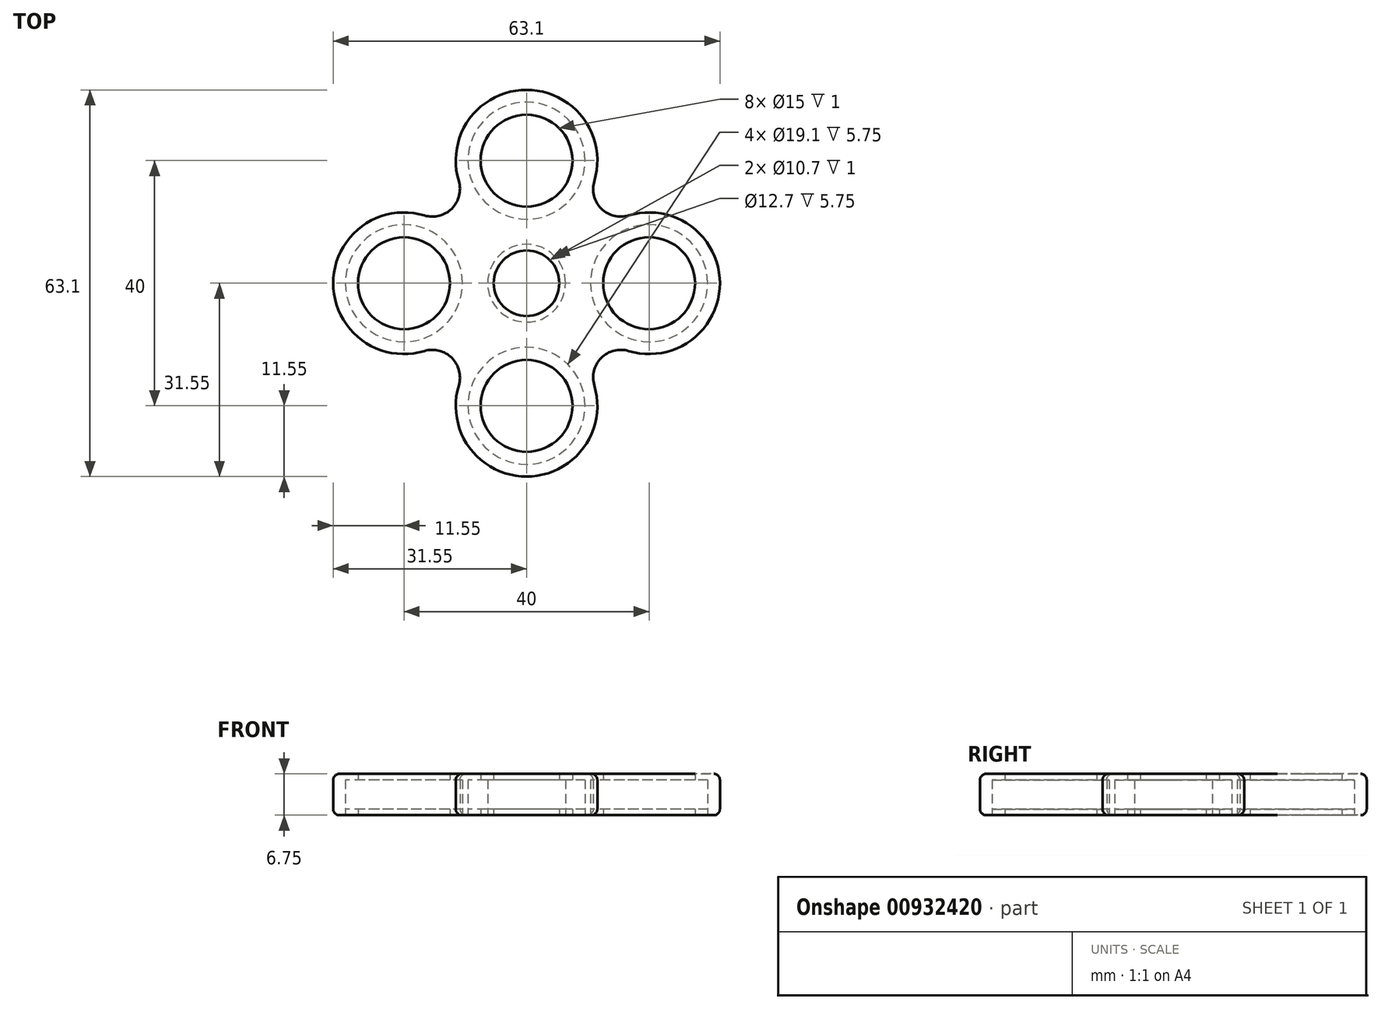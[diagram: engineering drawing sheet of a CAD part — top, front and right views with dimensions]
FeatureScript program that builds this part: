
annotation { "Feature Type Name" : "Feature", "Feature Type Description" : "" }
export const myFeature = defineFeature(function(context is Context, id is Id, definition is map)
    precondition{}
    {
        {
            var Q0;
            Q0=qCreatedBy(makeId("Top.planeOp"),FACE);
            var sketch = newSketch(context, id + "F0", { "sketchPlane" : qUnion([Q0])});
            skCircle(sketch, "E0", {"center": v(0, 0) * mm, "radius": 6.35 * mm});
            skCircle(sketch, "E1", {"center": v(0, 0) * mm, "radius": 5.35 * mm});
            skCircle(sketch, "E2.cCircle", {"center": v(0, 0) * mm, "radius": 20 * mm, "construction": true});
            skPoint(sketch, "E2.0.midPoint", {"position": v(20, 0) * mm});
            skCircle(sketch, "E3", {"center": v(-20, 0) * mm, "radius": 9.55 * mm});
            skCircle(sketch, "E4", {"center": v(0, 20) * mm, "radius": 9.55 * mm});
            skCircle(sketch, "E5", {"center": v(20, 0) * mm, "radius": 9.55 * mm});
            skCircle(sketch, "E6", {"center": v(0, -20) * mm, "radius": 9.55 * mm});
            skCircle(sketch, "E7", {"center": v(0, 20) * mm, "radius": 11.55 * mm});
            skCircle(sketch, "E8", {"center": v(-20, 0) * mm, "radius": 11.55 * mm});
            skCircle(sketch, "E9", {"center": v(0, -20) * mm, "radius": 11.55 * mm});
            skCircle(sketch, "E10", {"center": v(20, 0) * mm, "radius": 11.55 * mm});
            skArc(sketch, "E11", {"start": v(-16.66, 11.06) * mm, "mid": v(-12.18, 12.18) * mm, "end": v(-11.06, 16.66) * mm});
            skArc(sketch, "E12", {"start": v(-11.06, -16.66) * mm, "mid": v(-12.18, -12.18) * mm, "end": v(-16.66, -11.06) * mm});
            skArc(sketch, "E13", {"start": v(16.66, -11.06) * mm, "mid": v(12.18, -12.18) * mm, "end": v(11.06, -16.66) * mm});
            skArc(sketch, "E14", {"start": v(11.06, 16.66) * mm, "mid": v(12.18, 12.18) * mm, "end": v(16.66, 11.06) * mm});
            skPoint(sketch, "E15.orphan", {"position": v(-20, 20) * mm});
            skPoint(sketch, "E16.orphan", {"position": v(20, 20) * mm});
            skPoint(sketch, "E17.orphan", {"position": v(-20, -20) * mm});
            skPoint(sketch, "E18.orphan", {"position": v(20, -20) * mm});
            skCircle(sketch, "E19", {"center": v(0, 20) * mm, "radius": 7.5 * mm});
            skCircle(sketch, "E20", {"center": v(20, 0) * mm, "radius": 7.5 * mm});
            skCircle(sketch, "E21", {"center": v(0, -20) * mm, "radius": 7.5 * mm});
            skCircle(sketch, "E22", {"center": v(-20, 0) * mm, "radius": 7.5 * mm});
            skSolve(sketch);
        }
        {
            var Q0;
            Q0=makeQuery(id+"F0.imprint","IMPRINT",FACE,{"disambiguationData":[TD([[makeQuery(id+"F0.imprint","IMPRINT",EDGE,{"derivedFrom":sQuery(id+"F0.wireOp",EDGE,"E3")}),1.0]])]});
            var Q1;
            Q1=makeQuery(id+"F0.imprint","IMPRINT",FACE,{"disambiguationData":[TD([[makeQuery(id+"F0.imprint","IMPRINT",EDGE,{"derivedFrom":sQuery(id+"F0.wireOp",EDGE,"E4")}),1.0]])]});
            var Q2;
            Q2=makeQuery(id+"F0.imprint","IMPRINT",FACE,{"disambiguationData":[TD([[makeQuery(id+"F0.imprint","IMPRINT",EDGE,{"derivedFrom":sQuery(id+"F0.wireOp",EDGE,"E5")}),1.0]])]});
            var Q3;
            Q3=makeQuery(id+"F0.imprint","IMPRINT",FACE,{"disambiguationData":[TD([[makeQuery(id+"F0.imprint","IMPRINT",EDGE,{"derivedFrom":sQuery(id+"F0.wireOp",EDGE,"E6")}),1.0]])]});
            var Q4;
            Q4=makeQuery(id+"F0.imprint","IMPRINT",FACE,{"disambiguationData":[TD([[makeQuery(id+"F0.imprint","IMPRINT",EDGE,{"derivedFrom":sQuery(id+"F0.wireOp",EDGE,"E0")}),1.0]])]});
            extrude(context, id + "F1", {"entities" : qUnion([Q0, Q1, Q2, Q3, Q4]), "depth" : 1 * mm, "offsetDistance" : 25 * mm});
        }
        {
            var Q0;
            Q0=makeQuery(id+"F0.imprint","IMPRINT",FACE,{"disambiguationData":[TD([[makeQuery(id+"F0.imprint","IMPRINT",EDGE,{"derivedFrom":sQuery(id+"F0.wireOp",EDGE,"E0")}),-1.0]])]});
            var Q1;
            Q1=makeQuery(id+"F0.imprint","IMPRINT",FACE,{"disambiguationData":[TD([[makeQuery(id+"F0.imprint","IMPRINT",EDGE,{"derivedFrom":sQuery(id+"F0.wireOp",EDGE,"E3")}),-1.0]])]});
            var Q2;
            Q2=makeQuery(id+"F0.imprint","IMPRINT",FACE,{"disambiguationData":[TD([[makeQuery(id+"F0.imprint","IMPRINT",EDGE,{"derivedFrom":sQuery(id+"F0.wireOp",EDGE,"E4")}),-1.0]])]});
            var Q3;
            Q3=makeQuery(id+"F0.imprint","IMPRINT",FACE,{"disambiguationData":[TD([[makeQuery(id+"F0.imprint","IMPRINT",EDGE,{"derivedFrom":sQuery(id+"F0.wireOp",EDGE,"E5")}),-1.0]])]});
            var Q4;
            Q4=makeQuery(id+"F0.imprint","IMPRINT",FACE,{"disambiguationData":[TD([[makeQuery(id+"F0.imprint","IMPRINT",EDGE,{"derivedFrom":sQuery(id+"F0.wireOp",EDGE,"E6")}),-1.0]])]});
            extrude(context, id + "F2", {"entities" : qUnion([Q0, Q1, Q2, Q3, Q4]), "depth" : 6.75 * mm, "offsetDistance" : 25 * mm});
        }
        {
            var Q0;
            Q0=makeQuery(id+"F2.opExtrude","CAP_EDGE",EDGE,{"disambiguationData":[OSD([sQuery(id+"F0.wireOp",EDGE,"E11")])],"isStart":true});
            var Q1;
            Q1=makeQuery(id+"F2.opExtrude","CAP_EDGE",EDGE,{"disambiguationData":[OSD([sQuery(id+"F0.wireOp",EDGE,"E8")])],"isStart":true});
            var Q2;
            Q2=makeQuery(id+"F2.opExtrude","CAP_EDGE",EDGE,{"disambiguationData":[OSD([sQuery(id+"F0.wireOp",EDGE,"E12")])],"isStart":true});
            var Q3;
            Q3=makeQuery(id+"F2.opExtrude","CAP_EDGE",EDGE,{"disambiguationData":[OSD([sQuery(id+"F0.wireOp",EDGE,"E9")])],"isStart":true});
            var Q4;
            Q4=makeQuery(id+"F2.opExtrude","CAP_EDGE",EDGE,{"disambiguationData":[OSD([sQuery(id+"F0.wireOp",EDGE,"E13")])],"isStart":true});
            var Q5;
            Q5=makeQuery(id+"F2.opExtrude","CAP_EDGE",EDGE,{"disambiguationData":[OSD([sQuery(id+"F0.wireOp",EDGE,"E10")])],"isStart":true});
            var Q6;
            Q6=makeQuery(id+"F2.opExtrude","CAP_EDGE",EDGE,{"disambiguationData":[OSD([sQuery(id+"F0.wireOp",EDGE,"E14")])],"isStart":true});
            var Q7;
            Q7=makeQuery(id+"F2.opExtrude","CAP_EDGE",EDGE,{"disambiguationData":[OSD([sQuery(id+"F0.wireOp",EDGE,"E7")])],"isStart":true});
            var Q8;
            Q8=makeQuery(id+"F2.opExtrude","CAP_EDGE",EDGE,{"disambiguationData":[OSD([sQuery(id+"F0.wireOp",EDGE,"E9")])],"isStart":false});
            fillet(context, id + "F3", {"entities" : qUnion([Q0, Q1, Q2, Q3, Q4, Q5, Q6, Q7, Q8]), "radius" : 1 * mm, "tangentPropagation" : true, "allowEdgeOverflow" : false});
        }
        {
            var Q0;
            Q0=makeQuery(id+"F1.opExtrude","CAP_FACE",FACE,{"disambiguationData":[OSD([sQuery(id+"F0.wireOp",EDGE,"E0"),sQuery(id+"F0.wireOp",EDGE,"E1")])],"isStart":false});
            var Q1;
            Q1=makeQuery(id+"F2.opExtrude","CAP_FACE",FACE,{"disambiguationData":[OSD([sQuery(id+"F0.wireOp",EDGE,"E0"),sQuery(id+"F0.wireOp",EDGE,"E3"),sQuery(id+"F0.wireOp",EDGE,"E4"),sQuery(id+"F0.wireOp",EDGE,"E5"),sQuery(id+"F0.wireOp",EDGE,"E6"),sQuery(id+"F0.wireOp",EDGE,"E7"),sQuery(id+"F0.wireOp",EDGE,"E8"),sQuery(id+"F0.wireOp",EDGE,"E9"),sQuery(id+"F0.wireOp",EDGE,"E10"),sQuery(id+"F0.wireOp",EDGE,"E11"),sQuery(id+"F0.wireOp",EDGE,"E12"),sQuery(id+"F0.wireOp",EDGE,"E13"),sQuery(id+"F0.wireOp",EDGE,"E14")])],"isStart":false});
            extrude(context, id + "F4", {"entities" : qUnion([Q0]), "operationType" : NewBodyOperationType.ADD, "oppositeDirection" : true, "depth" : -5.75 * mm, "endBoundEntityFace" : qUnion([Q1]), "offsetDistance" : 25 * mm, "hasSecondDirection" : true, "secondDirectionOppositeDirection" : true, "secondDirectionDepth" : -4.75 * mm});
        }
        {
            var Q0;
            Q0=makeQuery(id+"F1.opExtrude","CAP_FACE",FACE,{"disambiguationData":[OSD([sQuery(id+"F0.wireOp",EDGE,"E4"),sQuery(id+"F0.wireOp",EDGE,"E19")])],"isStart":false});
            var Q1;
            Q1=makeQuery(id+"F1.opExtrude","CAP_FACE",FACE,{"disambiguationData":[OSD([sQuery(id+"F0.wireOp",EDGE,"E5"),sQuery(id+"F0.wireOp",EDGE,"E20")])],"isStart":false});
            var Q2;
            Q2=makeQuery(id+"F1.opExtrude","CAP_FACE",FACE,{"disambiguationData":[OSD([sQuery(id+"F0.wireOp",EDGE,"E6"),sQuery(id+"F0.wireOp",EDGE,"E21")])],"isStart":false});
            var Q3;
            Q3=makeQuery(id+"F1.opExtrude","CAP_FACE",FACE,{"disambiguationData":[OSD([sQuery(id+"F0.wireOp",EDGE,"E3"),sQuery(id+"F0.wireOp",EDGE,"E22")])],"isStart":false});
            extrude(context, id + "F5", {"entities" : qUnion([Q0, Q1, Q2, Q3]), "operationType" : NewBodyOperationType.ADD, "oppositeDirection" : true, "depth" : -5.75 * mm, "offsetDistance" : 25 * mm, "hasSecondDirection" : true, "secondDirectionOppositeDirection" : true, "secondDirectionDepth" : -4.75 * mm});
        }
    });
